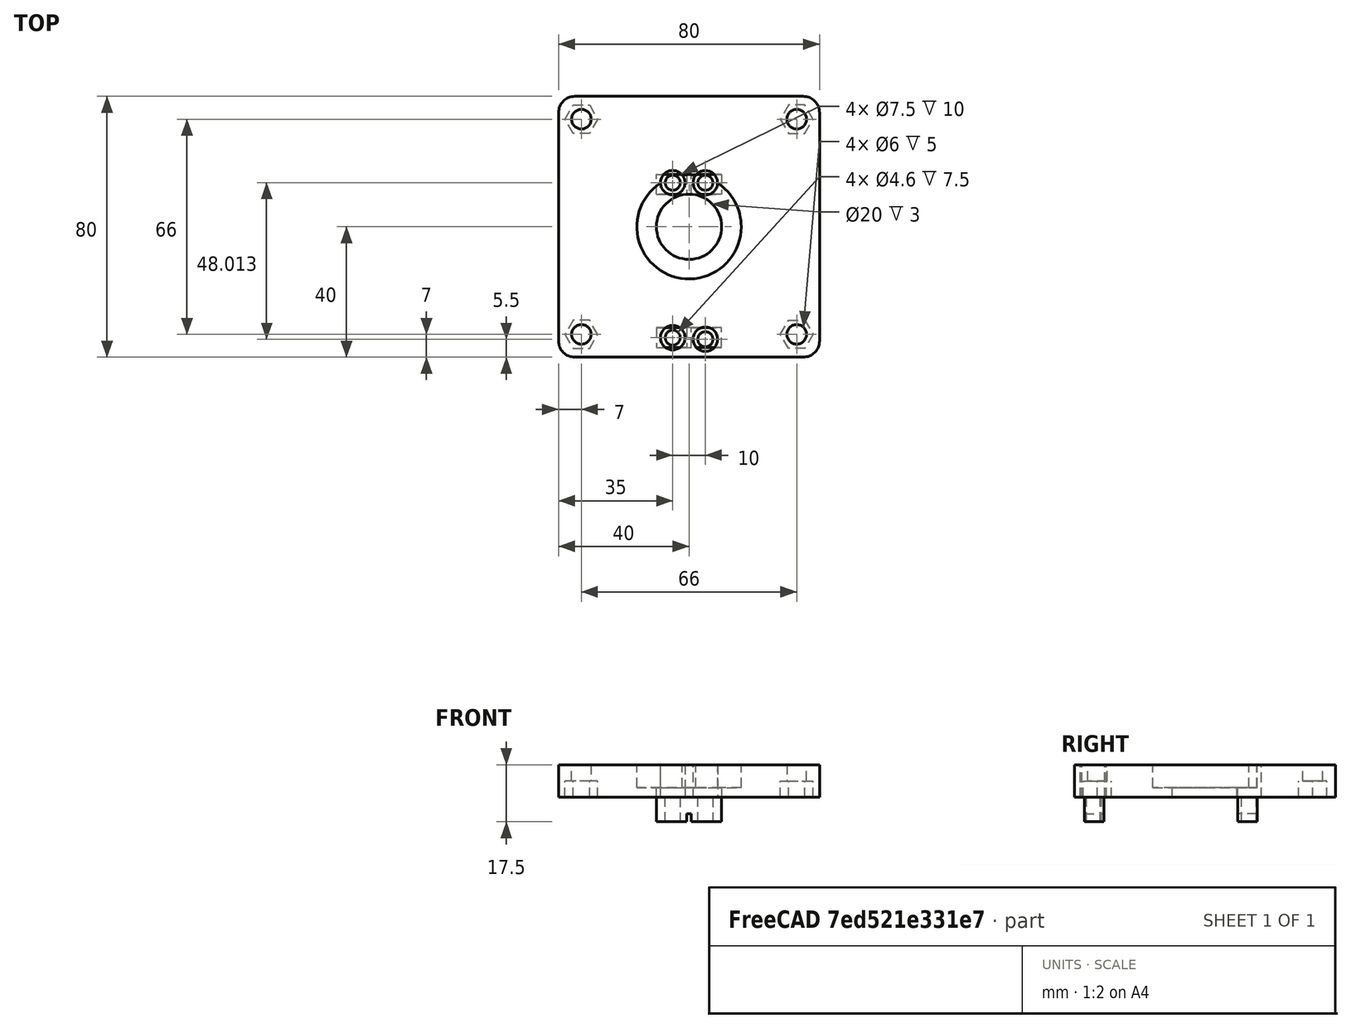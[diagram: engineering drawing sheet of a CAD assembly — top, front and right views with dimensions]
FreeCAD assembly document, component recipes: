
FREECAD ASSEMBLY — COMPONENT RECIPES ("Base_Plate")

This assembly document has 2 components, labeled P0..P1 below (a component is one placed body or linked part). 2 of them carry a construction recipe — the FreeCAD feature program that regenerates the part from scratch, quoted from this document or its linked companion documents; the rest are supplied as boundary geometry only. No exploded tour is included for this assembly.
COMPONENT P0 — recipe-attached ("Link001(Ball_Bearing)", modeled in this document).
Construction recipe (the document's own serialized feature program — sketch geometry with constraints, then the solid features built on it; lengths are millimeters unless a unit is written):

FEATURE [Sketcher::SketchObject] Sketch
  ArcFitTolerance = 1e-06
  AttachmentSupport = -> [XY_Plane]
  ExternalBSplineMaxDegree = 5
  ExternalBSplineTolerance = 0.0001
  FullyConstrained = true
  InternalTolerance = 1e-06
  InvalidShape = false
  MakeInternals = false
  MapMode = 5
  Support = -> [XY_Plane]
  TreeRank = 18
  ValidateShape = false
  sketch-geometry (5):
    g0: LineSegment StartX=-40 StartY=-40 StartZ=0 EndX=-40 EndY=40 EndZ=0
    g1: LineSegment StartX=-40 StartY=40 StartZ=0 EndX=40 EndY=40 EndZ=0
    g2: LineSegment StartX=40 StartY=40 StartZ=0 EndX=40 EndY=-40 EndZ=0
    g3: LineSegment StartX=40 StartY=-40 StartZ=0 EndX=-40 EndY=-40 EndZ=0
    g4: GeomPoint [constr] X=0 Y=0 Z=0
  constraints (12):
    c: Coincident(g0,g1)
    c: Coincident(g1,g2)
    c: Coincident(g2,g3)
    c: Coincident(g3,g0)
    c: Horizontal(g1)
    c: Horizontal(g3)
    c: Vertical(g0)
    c: Vertical(g2)
    c: Symmetric(g1,g0,g4)
    c: Coincident(g4,g-1)
    c: Distance(g1) = 80
    c: Equal(g2,g1)
FEATURE [PartDesign::Pad] Pad
  AddSubType = 0
  AlongSketchNormal = false
  AutoTaperInnerAngle = true
  CheckUpToFaceLimits = true
  ClaimChildren = false
  Direction = (0,0,1)
  Fit = 0
  FitJoin = 0
  InnerFit = 0
  InnerFitJoin = 0
  InvalidShape = false
  Length = 10
  Length2 = 10
  Linearize = true
  NewSolid = false
  Profile = -> Sketch
  ReferenceAxis = -> Sketch [N_Axis]
  Refine = true
  Suppress = false
  TaperInnerAngle = 0
  TaperInnerAngleRev = 0
  TreeRank = 19
  Type = 0
  ValidateShape = true
  _ProfileBasedVersion = 1
FEATURE [Sketcher::SketchObject] Sketch001
  ArcFitTolerance = 1e-06
  AttachmentSupport = -> [Pad]
  ExternalBSplineMaxDegree = 5
  ExternalBSplineTolerance = 0.0001
  FullyConstrained = true
  InternalTolerance = 1e-06
  InvalidShape = false
  MakeInternals = false
  MapMode = 5
  Placement = pos=(0,0,10) rot=(0,0,1;0rad)
  Support = -> [Pad]
  TreeRank = 20
  ValidateShape = false
  sketch-geometry (2):
    g0: Circle CenterX=0 CenterY=0 CenterZ=0 NormalX=0 NormalY=0 NormalZ=1 AngleXU=0 Radius=10
    g1: Circle CenterX=0 CenterY=0 CenterZ=0 NormalX=0 NormalY=0 NormalZ=1 AngleXU=0 Radius=16
  constraints (4):
    c: Coincident(g0,g-1)
    c: Diameter(g0) = 20
    c: Coincident(g1,g0)
    c: Diameter(g1) = 32
FEATURE [PartDesign::Pocket] Pocket
  AddSubType = 1
  AlongSketchNormal = false
  AutoTaperInnerAngle = true
  BaseFeature = -> Pad
  CheckUpToFaceLimits = true
  ClaimChildren = false
  Direction = (0,0,-1)
  Fit = 0
  FitJoin = 0
  InnerFit = 0
  InnerFitJoin = 0
  InvalidShape = false
  Length = 7
  Length2 = 10
  Linearize = true
  NewSolid = false
  Profile = -> Sketch001 [Edge2]
  ReferenceAxis = -> Sketch001 [N_Axis]
  Refine = true
  Suppress = false
  TaperInnerAngle = 0
  TaperInnerAngleRev = 0
  TreeRank = 21
  Type = 0
  ValidateShape = true
  _ProfileBasedVersion = 1
  _Version = 1
FEATURE [PartDesign::Pocket] Pocket001
  AddSubType = 1
  AlongSketchNormal = false
  AutoTaperInnerAngle = true
  BaseFeature = -> Pocket
  CheckUpToFaceLimits = true
  ClaimChildren = false
  Direction = (0,0,-1)
  Fit = 0
  FitJoin = 0
  InnerFit = 0
  InnerFitJoin = 0
  InvalidShape = false
  Length = 5
  Length2 = 10
  Linearize = true
  NewSolid = false
  Profile = -> Sketch001 [Edge1]
  ReferenceAxis = -> Sketch001 [N_Axis]
  Refine = true
  Suppress = false
  TaperInnerAngle = 0
  TaperInnerAngleRev = 0
  TreeRank = 22
  Type = 1
  ValidateShape = true
  _ProfileBasedVersion = 1
  _Version = 1
FEATURE [PartDesign::Fillet] Fillet
  AddSubType = 0
  Base = -> Pocket001 [Edge1,Edge5,Edge8,Edge2]
  BaseFeature = -> Pocket001
  InvalidShape = false
  NewSolid = false
  Radius = 5
  Refine = true
  SupportTransform = false
  Suppress = false
  TreeRank = 23
  UseAllEdges = false
  ValidateShape = true
FEATURE [Sketcher::SketchObject] Sketch002
  ArcFitTolerance = 1e-06
  AttachmentSupport = -> [Fillet]
  ExternalBSplineMaxDegree = 5
  ExternalBSplineTolerance = 0.0001
  ExternalGeometry = -> [Fillet]
  FullyConstrained = true
  InternalTolerance = 1e-06
  InvalidShape = false
  MakeInternals = false
  MapMode = 5
  Placement = pos=(0,0,10) rot=(0,0,1;0rad)
  Support = -> [Fillet]
  TreeRank = 24
  ValidateShape = false
  sketch-geometry (3):
    g0: Circle CenterX=-33 CenterY=33 CenterZ=0 NormalX=0 NormalY=0 NormalZ=1 AngleXU=0 Radius=3
    g1: LineSegment [constr] StartX=-33 StartY=33 StartZ=0 EndX=-33 EndY=40 EndZ=0
    g2: LineSegment [constr] StartX=-33 StartY=33 StartZ=0 EndX=-40 EndY=33 EndZ=0
  constraints (9):
    c: Diameter(g0) = 6
    c: Coincident(g1,g0)
    c: PointOnObject(g1,g-4)
    c: Vertical(g1)
    c: Coincident(g2,g0)
    c: PointOnObject(g2,g-3)
    c: Horizontal(g2)
    c: Equal(g2,g1)
    c: Distance(g1) = 7
FEATURE [PartDesign::Pocket] Pocket002
  AddSubType = 1
  AlongSketchNormal = false
  AutoTaperInnerAngle = true
  BaseFeature = -> Fillet
  CheckUpToFaceLimits = true
  ClaimChildren = false
  Direction = (0,0,-1)
  Fit = 0
  FitJoin = 0
  InnerFit = 0
  InnerFitJoin = 0
  InvalidShape = false
  Length = 5
  Length2 = 10
  Linearize = true
  NewSolid = false
  Profile = -> Sketch002 [Edge1]
  ReferenceAxis = -> Sketch002 [N_Axis]
  Refine = true
  Suppress = false
  TaperInnerAngle = 0
  TaperInnerAngleRev = 0
  TreeRank = 25
  Type = 1
  ValidateShape = true
  _ProfileBasedVersion = 1
  _Version = 1
FEATURE [Sketcher::SketchObject] Sketch003
  ArcFitTolerance = 1e-06
  AttachmentSupport = -> [Pocket002]
  ExternalBSplineMaxDegree = 5
  ExternalBSplineTolerance = 0.0001
  ExternalGeometry = -> [Pocket002]
  FullyConstrained = true
  InternalTolerance = 1e-06
  InvalidShape = false
  MakeInternals = false
  MapMode = 5
  Placement = pos=(0,0,0) rot=(1,0,0;3.14159rad)
  Support = -> [Pocket002]
  TreeRank = 26
  ValidateShape = false
  sketch-geometry (7):
    g0: LineSegment StartX=-30.5 StartY=-28.6699 StartZ=0 EndX=-35.5 EndY=-28.6699 EndZ=0
    g1: LineSegment StartX=-35.5 StartY=-28.6699 StartZ=0 EndX=-38 EndY=-33 EndZ=0
    g2: LineSegment StartX=-38 StartY=-33 StartZ=0 EndX=-35.5 EndY=-37.3301 EndZ=0
    g3: LineSegment StartX=-35.5 StartY=-37.3301 StartZ=0 EndX=-30.5 EndY=-37.3301 EndZ=0
    g4: LineSegment StartX=-30.5 StartY=-37.3301 StartZ=0 EndX=-28 EndY=-33 EndZ=0
    g5: LineSegment StartX=-28 StartY=-33 StartZ=0 EndX=-30.5 EndY=-28.6699 EndZ=0
    g6: Circle [constr] CenterX=-33 CenterY=-33 CenterZ=0 NormalX=0 NormalY=0 NormalZ=1 AngleXU=0 Radius=5
  constraints (16):
    c: Coincident(g0,g1)
    c: Coincident(g1,g2)
    c: Coincident(g2,g3)
    c: Coincident(g3,g4)
    c: Coincident(g4,g5)
    c: Coincident(g5,g0)
    c: Equal(g0, g1-g5) x5
    c: PointOnObject(g0,g6)
    c: PointOnObject(g1,g6)
    c: PointOnObject(g2,g6)
    c: PointOnObject(g3,g6)
    c: PointOnObject(g4,g6)
    c: PointOnObject(g5,g6)
    c: Coincident(g6,g-3)
    c: Horizontal(g0)
    c: Diameter(g6) = 10
FEATURE [PartDesign::Pocket] Pocket003
  AddSubType = 1
  AlongSketchNormal = false
  AutoTaperInnerAngle = true
  BaseFeature = -> Pocket002
  CheckUpToFaceLimits = true
  ClaimChildren = false
  Direction = (0,0,1)
  Fit = 0
  FitJoin = 0
  InnerFit = 0
  InnerFitJoin = 0
  InvalidShape = false
  Length = 5
  Length2 = 10
  Linearize = true
  NewSolid = false
  Profile = -> Sketch003
  ReferenceAxis = -> Sketch003 [N_Axis]
  Refine = true
  Suppress = false
  TaperInnerAngle = 0
  TaperInnerAngleRev = 0
  TreeRank = 27
  Type = 0
  ValidateShape = true
  _ProfileBasedVersion = 1
  _Version = 1
FEATURE [PartDesign::Mirrored] Mirrored
  AddSubType = 0
  BaseFeature = -> Pocket003
  CopyShape = false
  InvalidShape = false
  MirrorPlane = -> Sketch003 [V_Axis]
  NewSolid = false
  OriginalSubs = -> [Pocket003,Pocket002]
  Originals = -> [Pocket003,Pocket002]
  ParallelTransform = true
  Refine = true
  SubTransform = true
  Suppress = false
  TreeRank = 28
  ValidateShape = true
  _Version = 3
FEATURE [PartDesign::Mirrored] Mirrored001
  AddSubType = 0
  BaseFeature = -> Mirrored
  CopyShape = false
  InvalidShape = false
  MirrorPlane = -> XZ_Plane
  NewSolid = false
  OriginalSubs = -> [Mirrored,Pocket003,Pocket002]
  Originals = -> [Mirrored,Pocket003,Pocket002]
  ParallelTransform = true
  Refine = true
  SubTransform = true
  Suppress = false
  TreeRank = 29
  ValidateShape = true
  _Version = 3
FEATURE [Part::SubShapeBinder] Import  label="Import(*Hitec_D625MW001)"
  BindCopyOnChange = 0
  BindMode = 0
  ClaimChildren = false
  Context = -> Assembly [Parts.Part.Body.Import.]
  EdgeTolerance = 1e-06
  FillStyle = 0
  Fuse = false
  InvalidShape = false
  MakeFace = false
  MergeEdges = true
  OffsetFill = false
  OffsetIntersection = false
  OffsetJoinType = 0
  OffsetOpenResult = false
  Outline = false
  PartialLoad = false
  Relative = true
  SplitEdges = false
  Support = -> [Binder]
  TightBound = false
  TreeRank = 68
  ValidateShape = false
  _Version = 8
FEATURE [Sketcher::SketchObject] Sketch004
  ArcFitTolerance = 1e-06
  AttachmentSupport = -> [Mirrored001]
  ExternalBSplineMaxDegree = 5
  ExternalBSplineTolerance = 0.0001
  ExternalGeometry = -> [Import,Mirrored001]
  FullyConstrained = true
  InternalTolerance = 1e-06
  InvalidShape = false
  MakeInternals = false
  MapMode = 5
  Placement = pos=(0,0,0) rot=(1,0,0;3.14159rad)
  Support = -> [Mirrored001]
  TreeRank = 66
  ValidateShape = false
  sketch-geometry (8):
    g0: LineSegment StartX=-10 StartY=37 StartZ=0 EndX=10 EndY=37 EndZ=0
    g1: LineSegment StartX=10 StartY=37 StartZ=0 EndX=10 EndY=31 EndZ=0
    g2: LineSegment StartX=10 StartY=31 StartZ=0 EndX=-10 EndY=31 EndZ=0
    g3: LineSegment StartX=-10 StartY=31 StartZ=0 EndX=-10 EndY=37 EndZ=0
    g4: LineSegment StartX=-10 StartY=-16 StartZ=0 EndX=10 EndY=-16 EndZ=0
    g5: LineSegment StartX=10 StartY=-16 StartZ=0 EndX=10 EndY=-10 EndZ=0
    g6: LineSegment StartX=10 StartY=-10 StartZ=0 EndX=-10 EndY=-10 EndZ=0
    g7: LineSegment StartX=-10 StartY=-10 StartZ=0 EndX=-10 EndY=-16 EndZ=0
  constraints (24):
    c: Coincident(g0,g1)
    c: Coincident(g1,g2)
    c: Coincident(g2,g3)
    c: Coincident(g3,g0)
    c: Horizontal(g0)
    c: Horizontal(g2)
    c: Vertical(g1)
    c: Vertical(g3)
    c: PointOnObject(g-8,g0)
    c: Vertical(g1,g-5)
    c: Vertical(g2,g-4)
    c: Distance(g-3,g2) = 0.5
    c: Coincident(g4,g5)
    c: Coincident(g5,g6)
    c: Coincident(g6,g7)
    c: Coincident(g7,g4)
    c: Horizontal(g4)
    c: Horizontal(g6)
    c: Vertical(g5)
    c: Vertical(g7)
    c: Distance(g-6,g6) = 0.5
    c: PointOnObject(g-7,g4)
    c: Vertical(g6,g-4)
    c: Vertical(g5,g-5)
FEATURE [PartDesign::Pad] Pad001
  AddSubType = 0
  AlongSketchNormal = false
  AutoTaperInnerAngle = true
  BaseFeature = -> Mirrored001
  CheckUpToFaceLimits = true
  ClaimChildren = false
  Direction = (0,0,-1)
  Fit = 0
  FitJoin = 0
  InnerFit = 0
  InnerFitJoin = 0
  InvalidShape = false
  Length = 10
  Length2 = 10
  Linearize = true
  NewSolid = false
  Profile = -> Sketch004
  ReferenceAxis = -> Sketch004 [N_Axis]
  Refine = true
  Suppress = false
  TaperInnerAngle = 0
  TaperInnerAngleRev = 0
  TreeRank = 69
  Type = 3
  UpToFace = -> Import [Face4]
  ValidateShape = true
  _ProfileBasedVersion = 1
FEATURE [PartDesign::Plane] DatumPlane
  AttachmentSupport = -> [Pad001]
  InvalidShape = false
  Length = 80
  MapMode = 45
  MinimumLength = 10
  MinimumWidth = 10
  Placement = pos=(1.02103e-09,-10.5,-7.5) rot=(0,0,1;0rad)
  ResizeMode = 0
  Support = -> [Pad001]
  TreeRank = 70
  ValidateShape = false
  Width = 80
FEATURE [Sketcher::SketchObject] Sketch005
  ArcFitTolerance = 1e-06
  AttachmentSupport = -> [DatumPlane]
  ExternalBSplineMaxDegree = 5
  ExternalBSplineTolerance = 0.0001
  ExternalGeometry = -> [Import,Pad001]
  FullyConstrained = true
  InternalTolerance = 1e-06
  InvalidShape = false
  MakeInternals = false
  MapMode = 5
  Placement = pos=(1.02103e-09,-10.5,-7.5) rot=(0,0,1;0rad)
  Support = -> [DatumPlane]
  TreeRank = 71
  ValidateShape = false
  sketch-geometry (8):
    g0: LineSegment StartX=-0.725 StartY=-26.5 StartZ=0 EndX=0.725 EndY=-26.5 EndZ=0
    g1: LineSegment StartX=0.725 StartY=-26.5 StartZ=0 EndX=0.725 EndY=-20.5 EndZ=0
    g2: LineSegment StartX=0.725 StartY=-20.5 StartZ=0 EndX=-0.725 EndY=-20.5 EndZ=0
    g3: LineSegment StartX=-0.725 StartY=-20.5 StartZ=0 EndX=-0.725 EndY=-26.5 EndZ=0
    g4: LineSegment StartX=-0.725 StartY=20.5 StartZ=0 EndX=0.725 EndY=20.5 EndZ=0
    g5: LineSegment StartX=0.725 StartY=20.5 StartZ=0 EndX=0.725 EndY=26.5 EndZ=0
    g6: LineSegment StartX=0.725 StartY=26.5 StartZ=0 EndX=-0.725 EndY=26.5 EndZ=0
    g7: LineSegment StartX=-0.725 StartY=26.5 StartZ=0 EndX=-0.725 EndY=20.5 EndZ=0
  constraints (22):
    c: Coincident(g0,g1)
    c: Coincident(g1,g2)
    c: Coincident(g2,g3)
    c: Coincident(g3,g0)
    c: Horizontal(g2)
    c: Vertical(g1)
    c: Vertical(g3)
    c: PointOnObject(g0,g-10)
    c: PointOnObject(g1,g-9)
    c: Coincident(g4,g5)
    c: Coincident(g5,g6)
    c: Coincident(g6,g7)
    c: Coincident(g7,g4)
    c: Horizontal(g6)
    c: Vertical(g5)
    c: Vertical(g7)
    c: PointOnObject(g4,g-7)
    c: PointOnObject(g5,g-8)
    c: Symmetric(g4,g4,g-2)
    c: Distance(g-4,g5) = 0.1
    c: Symmetric(g0,g0,g-2)
    c: Distance(g-5,g0) = 0.1
FEATURE [PartDesign::Pocket] Pocket004
  AddSubType = 1
  AlongSketchNormal = false
  AutoTaperInnerAngle = true
  BaseFeature = -> Pad001
  CheckUpToFaceLimits = true
  ClaimChildren = false
  Direction = (0,0,-1)
  Fit = 0
  FitJoin = 0
  InnerFit = 0
  InnerFitJoin = 0
  InvalidShape = false
  Length = 2.5
  Length2 = 10
  Linearize = true
  NewSolid = false
  Profile = -> Sketch005
  ReferenceAxis = -> Sketch005 [N_Axis]
  Refine = true
  Reversed = true
  Suppress = false
  TaperInnerAngle = 0
  TaperInnerAngleRev = 0
  TreeRank = 72
  Type = 0
  ValidateShape = true
  _ProfileBasedVersion = 1
  _Version = 1
FEATURE [Sketcher::SketchObject] Sketch006
  ArcFitTolerance = 1e-06
  AttachmentSupport = -> [Pocket004]
  ExternalBSplineMaxDegree = 5
  ExternalBSplineTolerance = 0.0001
  ExternalGeometry = -> [Import]
  FullyConstrained = true
  InternalTolerance = 1e-06
  InvalidShape = false
  MakeInternals = false
  MapMode = 5
  Placement = pos=(0,0,10) rot=(0,0,1;0rad)
  Support = -> [Pocket004]
  TreeRank = 73
  ValidateShape = false
  sketch-geometry (4):
    g0: Circle CenterX=4.99999 CenterY=13.5 CenterZ=0 NormalX=0 NormalY=0 NormalZ=1 AngleXU=0 Radius=2.3
    g1: Circle CenterX=-5 CenterY=13.5126 CenterZ=0 NormalX=0 NormalY=0 NormalZ=1 AngleXU=0 Radius=2.3
    g2: Circle CenterX=-5 CenterY=-34.0222 CenterZ=0 NormalX=0 NormalY=0 NormalZ=1 AngleXU=0 Radius=2.3
    g3: Circle CenterX=5 CenterY=-34.5 CenterZ=0 NormalX=0 NormalY=0 NormalZ=1 AngleXU=0 Radius=2.3
  constraints (9):
    c: Coincident(g0,g-5)
    c: Coincident(g1,g-6)
    c: Coincident(g2,g-3)
    c: Coincident(g3,g-4)
    c: Equal(g0,g3)
    c: Equal(g3,g2)
    c: Equal(g2,g1)
    c: Radius(g-6) = 2.25
    c: Diameter(g1) = 4.6
FEATURE [PartDesign::Pocket] Pocket005
  AddSubType = 1
  AlongSketchNormal = false
  AutoTaperInnerAngle = true
  BaseFeature = -> Pocket004
  CheckUpToFaceLimits = true
  ClaimChildren = false
  Direction = (0,0,-1)
  Fit = 0
  FitJoin = 0
  InnerFit = 0
  InnerFitJoin = 0
  InvalidShape = false
  Length = 5
  Length2 = 10
  Linearize = true
  NewSolid = false
  Profile = -> Sketch006
  ReferenceAxis = -> Sketch006 [N_Axis]
  Refine = true
  Suppress = false
  TaperInnerAngle = 0
  TaperInnerAngleRev = 0
  TreeRank = 74
  Type = 1
  ValidateShape = true
  _ProfileBasedVersion = 1
  _Version = 1
FEATURE [Sketcher::SketchObject] Sketch007
  ArcFitTolerance = 1e-06
  AttachmentSupport = -> [Pocket005]
  ExternalBSplineMaxDegree = 5
  ExternalBSplineTolerance = 0.0001
  ExternalGeometry = -> [Pocket005]
  FullyConstrained = true
  InternalTolerance = 1e-06
  InvalidShape = false
  MakeInternals = false
  MapMode = 5
  Placement = pos=(0,0,10) rot=(0,0,1;0rad)
  Support = -> [Pocket005]
  TreeRank = 75
  ValidateShape = false
  sketch-geometry (4):
    g0: Circle CenterX=5 CenterY=-34.5 CenterZ=0 NormalX=0 NormalY=0 NormalZ=1 AngleXU=0 Radius=3.75
    g1: Circle CenterX=-5 CenterY=-34.0222 CenterZ=0 NormalX=0 NormalY=0 NormalZ=1 AngleXU=0 Radius=3.75
    g2: Circle CenterX=4.99999 CenterY=13.5 CenterZ=0 NormalX=0 NormalY=0 NormalZ=1 AngleXU=0 Radius=3.75
    g3: Circle CenterX=-5 CenterY=13.5126 CenterZ=0 NormalX=0 NormalY=0 NormalZ=1 AngleXU=0 Radius=3.75
  constraints (8):
    c: Coincident(g0,g-5)
    c: Coincident(g1,g-6)
    c: Coincident(g2,g-3)
    c: Coincident(g3,g-4)
    c: Equal(g0,g1)
    c: Equal(g1,g2)
    c: Equal(g2,g3)
    c: Diameter(g0) = 7.5
FEATURE [PartDesign::Pocket] Pocket006
  AddSubType = 1
  AlongSketchNormal = false
  AutoTaperInnerAngle = true
  BaseFeature = -> Pocket005
  CheckUpToFaceLimits = true
  ClaimChildren = false
  Direction = (0,0,-1)
  Fit = 0
  FitJoin = 0
  InnerFit = 0
  InnerFitJoin = 0
  InvalidShape = false
  Length = 0
  Length2 = 10
  Linearize = true
  NewSolid = false
  Offset = 3
  Profile = -> Sketch007
  ReferenceAxis = -> Sketch007 [N_Axis]
  Refine = true
  Suppress = false
  TaperInnerAngle = 0
  TaperInnerAngleRev = 0
  TreeRank = 76
  Type = 3
  UpToFace = -> Pocket005 [Face61]
  ValidateShape = true
  _ProfileBasedVersion = 1
  _Version = 1
FEATURE [PartDesign::Body] Body
  AutoGroupSolids = false
  ClaimAllChildren = false
  ExportMode = 0
  Group = -> [Sketch,Pad,Sketch001,Pocket,Pocket001,Fillet,Sketch002,Pocket002,Sketch003,Pocket003,Mirrored,Mirrored001,Sketch004,Import,Pad001,DatumPlane,Sketch005,Pocket004,Sketch006,Pocket005,Sketch007,Pocket006]
  InvalidShape = false
  Origin = -> Origin001
  Tip = -> Pocket006
  TreeRank = 17
  ValidateShape = false
  _ExportChildren = -> [Pad,Pocket,Pocket001,Fillet,Pocket002,Pocket003,Mirrored,Mirrored001,Import,Pad001,DatumPlane,Pocket004,Pocket005,Pocket006]
  _GroupVersion = 1
COMPONENT P1 — same part as P0; its construction recipe is shown at P0.
PROVENANCE & LICENSES
A FreeCAD (.FCStd) document from a public repository crawl; recipes are the document's own serialized feature recipes (and, for linked parts, companion documents' recipes).
License: gpl-3.0.
